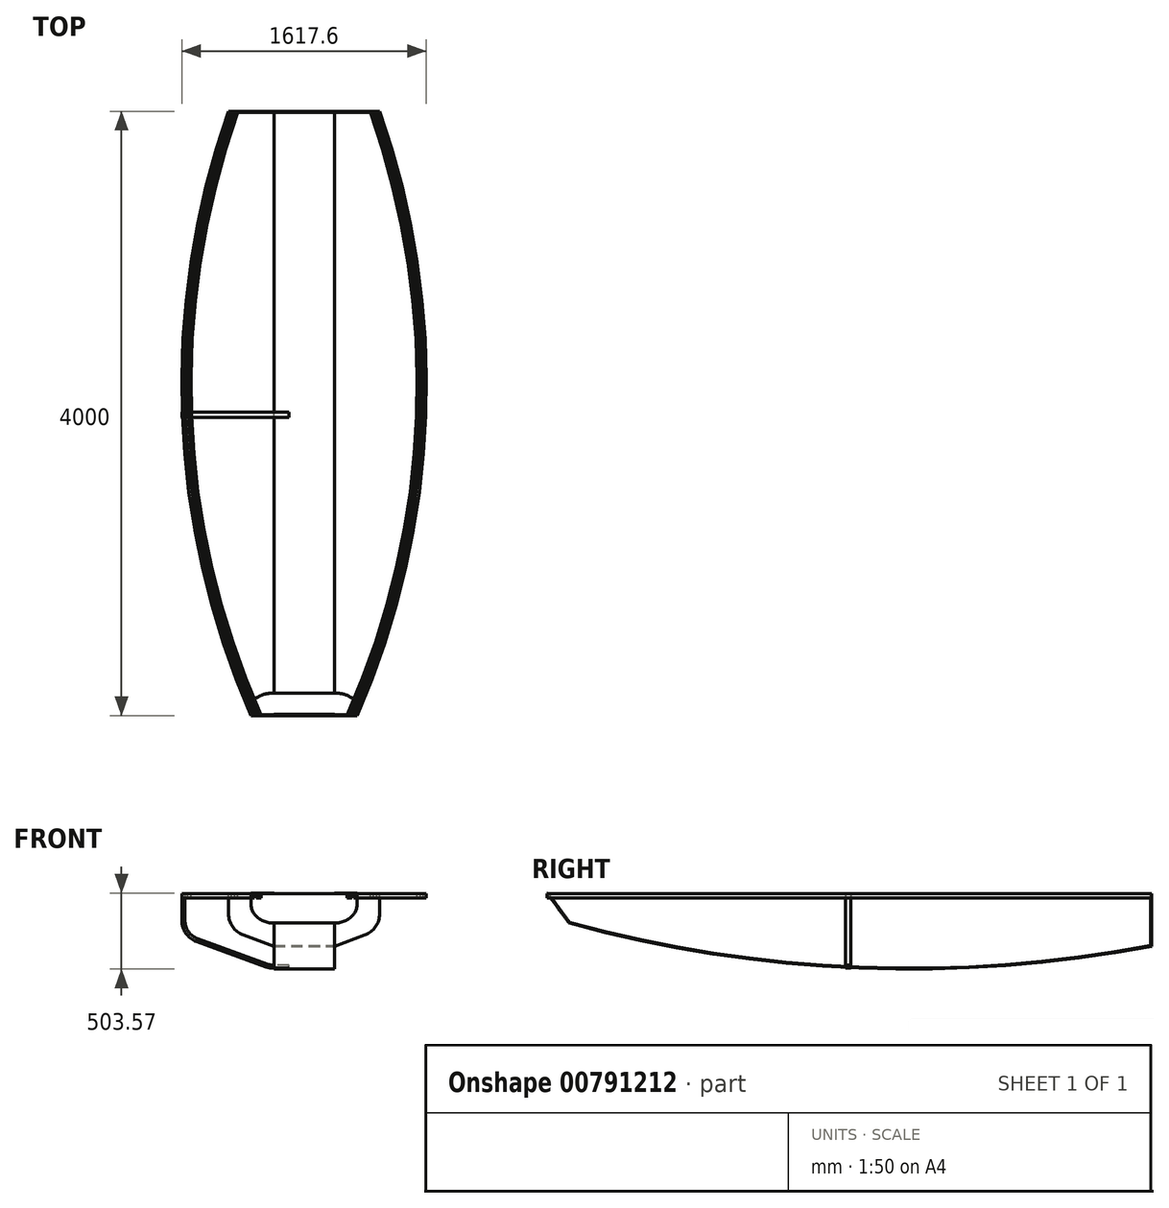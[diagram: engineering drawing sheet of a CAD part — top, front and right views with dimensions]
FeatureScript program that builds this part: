
annotation { "Feature Type Name" : "Feature", "Feature Type Description" : "" }
export const myFeature = defineFeature(function(context is Context, id is Id, definition is map)
    precondition{}
    {
        {
            var Q0;
            Q0=qCreatedBy(makeId("Right.planeOp"),FACE);
            var sketch = newSketch(context, id + "F0", { "sketchPlane" : qUnion([Q0])});
            skLineSegment(sketch, "E0.bottom", {"start": v(0, 0) * mm, "end": v(-4000, 0) * mm});
            skLineSegment(sketch, "E0.top", {"start": v(0, 500) * mm, "end": v(-4000, 500) * mm});
            skLineSegment(sketch, "E0.left", {"start": v(0, 0) * mm, "end": v(0, 500) * mm});
            skLineSegment(sketch, "E0.right", {"start": v(-4000, 0) * mm, "end": v(-4000, 500) * mm});
            skSolve(sketch);
        }
        {
            var Q0;
            Q0 = qSketchRegion(id + "F0", true);
            extrude(context, id + "F1", {"entities" : qUnion([Q0]), "depth" : 200 * mm, "offsetDistance" : 25 * mm, "hasSecondDirection" : true, "secondDirectionOppositeDirection" : true, "secondDirectionDepth" : 200 * mm});
        }
        {
            var Q0;
            Q0=makeQuery(id+"F1.opExtrude","CAP_FACE",FACE,{"disambiguationData":[OSD([sQuery(id+"F0.wireOp",EDGE,"E0.bottom"),sQuery(id+"F0.wireOp",EDGE,"E0.top"),sQuery(id+"F0.wireOp",EDGE,"E0.left"),sQuery(id+"F0.wireOp",EDGE,"E0.right")])],"isStart":false});
            var sketch = newSketch(context, id + "F2", { "sketchPlane" : qUnion([Q0])});
            skLineSegment(sketch, "E1.0", {"start": v(0, 0) * mm, "end": v(-4000, 0) * mm});
            skLineSegment(sketch, "E2.0", {"start": v(0, 0) * mm, "end": v(0, 151.95) * mm});
            skArc(sketch, "E3", {"start": v(-3855.38, 304.68) * mm, "mid": v(-1936.47, 6.66) * mm, "end": v(0, 151.95) * mm});
            skPoint(sketch, "E4.orphan", {"position": v(0, 500) * mm});
            skPoint(sketch, "E5.orphan", {"position": v(-4121.15, 382.5) * mm});
            skPoint(sketch, "E6.start.orphan", {"position": v(-4000, 500) * mm});
            skLineSegment(sketch, "E7", {"start": v(-4000, 500) * mm, "end": v(-4000, 0) * mm});
            skLineSegment(sketch, "E8", {"start": v(-3855.38, 304.68) * mm, "end": v(-4000, 500) * mm});
            skSolve(sketch);
        }
        {
            var Q0;
            Q0 = qSketchRegion(id + "F2", true);
            extrude(context, id + "F3", {"entities" : qUnion([Q0]), "operationType" : NewBodyOperationType.REMOVE, "endBound" : BoundingType.THROUGH_ALL, "oppositeDirection" : true, "depth" : 25 * mm, "offsetDistance" : 25 * mm});
        }
        {
            var Q0;
            Q0=makeQuery(id+"F1.opExtrude","CAP_FACE",FACE,{"disambiguationData":[OSD([sQuery(id+"F0.wireOp",EDGE,"E0.bottom"),sQuery(id+"F0.wireOp",EDGE,"E0.top"),sQuery(id+"F0.wireOp",EDGE,"E0.left"),sQuery(id+"F0.wireOp",EDGE,"E0.right")])],"isStart":false});
            var sketch = newSketch(context, id + "F4", { "sketchPlane" : qUnion([Q0])});
            skArc(sketch, "E9.0", {"start": v(-3851.8, 309.92) * mm, "mid": v(-1937.68, 12.71) * mm, "end": v(-6, 156.9) * mm});
            skLineSegment(sketch, "E10.0", {"start": v(-6, 156.9) * mm, "end": v(-6, 500) * mm});
            skLineSegment(sketch, "E11.0", {"start": v(-3851.8, 309.92) * mm, "end": v(-3992.53, 500) * mm});
            skLineSegment(sketch, "E12.0", {"start": v(-6, 500) * mm, "end": v(-3992.53, 500) * mm});
            skPoint(sketch, "E13.orphan", {"position": v(0, 500) * mm});
            skPoint(sketch, "E14.orphan", {"position": v(-4000, 500) * mm});
            skSolve(sketch);
        }
        {
            var Q0;
            Q0 = qSketchRegion(id + "F4", true);
            extrude(context, id + "F5", {"entities" : qUnion([Q0]), "operationType" : NewBodyOperationType.REMOVE, "endBound" : BoundingType.THROUGH_ALL, "oppositeDirection" : true, "depth" : 25 * mm, "offsetDistance" : 25 * mm});
        }
        {
            var Q0;
            Q0=qCreatedBy(makeId("Front.planeOp"),FACE);
            cPlane(context, id + "F6", {"entities" : qUnion([Q0]), "cplaneType" : CPlaneType.OFFSET, "offset" : 200 * mm, "width" : 150 * mm, "height" : 150 * mm});
        }
        {
            var Q0;
            Q0=qCreatedBy(id+"F6.planeOp",FACE);
            cPlane(context, id + "F7", {"entities" : qUnion([Q0]), "cplaneType" : CPlaneType.OFFSET, "offset" : 200 * mm, "width" : 150 * mm, "height" : 150 * mm});
        }
        {
            var Q0;
            Q0=qCreatedBy(id+"F7.planeOp",FACE);
            cPlane(context, id + "F8", {"entities" : qUnion([Q0]), "cplaneType" : CPlaneType.OFFSET, "offset" : 200 * mm, "width" : 150 * mm, "height" : 150 * mm});
        }
        {
            var Q0;
            Q0=qCreatedBy(id+"F8.planeOp",FACE);
            cPlane(context, id + "F9", {"entities" : qUnion([Q0]), "cplaneType" : CPlaneType.OFFSET, "offset" : 200 * mm, "width" : 150 * mm, "height" : 150 * mm});
        }
        {
            var Q0;
            Q0=qCreatedBy(id+"F9.planeOp",FACE);
            cPlane(context, id + "F10", {"entities" : qUnion([Q0]), "cplaneType" : CPlaneType.OFFSET, "offset" : 200 * mm, "width" : 150 * mm, "height" : 150 * mm});
        }
        {
            var Q0;
            Q0=qCreatedBy(id+"F10.planeOp",FACE);
            cPlane(context, id + "F11", {"entities" : qUnion([Q0]), "cplaneType" : CPlaneType.OFFSET, "offset" : 200 * mm, "width" : 150 * mm, "height" : 150 * mm});
        }
        {
            var Q0;
            Q0=qCreatedBy(id+"F11.planeOp",FACE);
            cPlane(context, id + "F12", {"entities" : qUnion([Q0]), "cplaneType" : CPlaneType.OFFSET, "offset" : 200 * mm, "width" : 150 * mm, "height" : 150 * mm});
        }
        {
            var Q0;
            Q0=qCreatedBy(id+"F12.planeOp",FACE);
            cPlane(context, id + "F13", {"entities" : qUnion([Q0]), "cplaneType" : CPlaneType.OFFSET, "offset" : 200 * mm, "width" : 150 * mm, "height" : 150 * mm});
        }
        {
            var Q0;
            Q0=qCreatedBy(id+"F13.planeOp",FACE);
            cPlane(context, id + "F14", {"entities" : qUnion([Q0]), "cplaneType" : CPlaneType.OFFSET, "offset" : 200 * mm, "width" : 150 * mm, "height" : 150 * mm});
        }
        {
            var Q0;
            Q0=qCreatedBy(id+"F14.planeOp",FACE);
            cPlane(context, id + "F15", {"entities" : qUnion([Q0]), "cplaneType" : CPlaneType.OFFSET, "offset" : 200 * mm, "width" : 150 * mm, "height" : 150 * mm});
        }
        {
            var Q0;
            Q0=qCreatedBy(id+"F15.planeOp",FACE);
            cPlane(context, id + "F16", {"entities" : qUnion([Q0]), "cplaneType" : CPlaneType.OFFSET, "offset" : 200 * mm, "width" : 150 * mm, "height" : 150 * mm});
        }
        {
            var Q0;
            Q0=qCreatedBy(id+"F16.planeOp",FACE);
            cPlane(context, id + "F17", {"entities" : qUnion([Q0]), "cplaneType" : CPlaneType.OFFSET, "offset" : 200 * mm, "width" : 150 * mm, "height" : 150 * mm});
        }
        {
            var Q0;
            Q0=qCreatedBy(id+"F17.planeOp",FACE);
            cPlane(context, id + "F18", {"entities" : qUnion([Q0]), "cplaneType" : CPlaneType.OFFSET, "offset" : 200 * mm, "width" : 150 * mm, "height" : 150 * mm});
        }
        {
            var Q0;
            Q0=qCreatedBy(id+"F18.planeOp",FACE);
            cPlane(context, id + "F19", {"entities" : qUnion([Q0]), "cplaneType" : CPlaneType.OFFSET, "offset" : 200 * mm, "width" : 150 * mm, "height" : 150 * mm});
        }
        {
            var Q0;
            Q0=qCreatedBy(id+"F19.planeOp",FACE);
            cPlane(context, id + "F20", {"entities" : qUnion([Q0]), "cplaneType" : CPlaneType.OFFSET, "offset" : 200 * mm, "width" : 150 * mm, "height" : 150 * mm});
        }
        {
            var Q0;
            Q0=qCreatedBy(id+"F20.planeOp",FACE);
            cPlane(context, id + "F21", {"entities" : qUnion([Q0]), "cplaneType" : CPlaneType.OFFSET, "offset" : 200 * mm, "width" : 150 * mm, "height" : 150 * mm});
        }
        {
            var Q0;
            Q0=qCreatedBy(id+"F21.planeOp",FACE);
            cPlane(context, id + "F22", {"entities" : qUnion([Q0]), "cplaneType" : CPlaneType.OFFSET, "offset" : 200 * mm, "width" : 150 * mm, "height" : 150 * mm});
        }
        {
            var Q0;
            Q0=qCreatedBy(id+"F22.planeOp",FACE);
            cPlane(context, id + "F23", {"entities" : qUnion([Q0]), "cplaneType" : CPlaneType.OFFSET, "offset" : 200 * mm, "width" : 150 * mm, "height" : 150 * mm});
        }
        {
            var Q0;
            Q0=qCreatedBy(makeId("Top.planeOp"),FACE);
            cPlane(context, id + "F24", {"entities" : qUnion([Q0]), "cplaneType" : CPlaneType.OFFSET, "offset" : 500 * mm, "width" : 150 * mm, "height" : 150 * mm});
        }
        {
            var Q0;
            Q0=makeQuery(id+"F3.boolean.opBoolean","COPY",FACE,{"derivedFrom":makeQuery(id+"F3.opExtrude","SWEPT_FACE",FACE,{"disambiguationData":[OSD([sQuery(id+"F2.wireOp",EDGE,"E8")])]})});
            var sketch = newSketch(context, id + "F25", { "sketchPlane" : qUnion([Q0])});
            skLineSegment(sketch, "E15.0.3", {"start": v(200, 2539.04) * mm, "end": v(-200, 2539.04) * mm});
            skLineSegment(sketch, "E16.0", {"start": v(-200, 2539.04) * mm, "end": v(-200, 2782.07) * mm});
            skLineSegment(sketch, "E17", {"start": v(-200, 2782.07) * mm, "end": v(-350, 2782.07) * mm});
            skPoint(sketch, "E15.0.1.end.orphan", {"position": v(200, 122.12) * mm});
            skPoint(sketch, "E15.0.1.start.orphan", {"position": v(-200, 122.12) * mm});
            skArc(sketch, "E18", {"start": v(-200, 2539.04) * mm, "mid": v(-306.07, 2582.97) * mm, "end": v(-350, 2689.04) * mm});
            skLineSegment(sketch, "E19", {"start": v(-200, 2689.04) * mm, "end": v(-440.1, 2689.04) * mm, "construction": true});
            skLineSegment(sketch, "E20", {"start": v(-350, 2689.04) * mm, "end": v(-350, 2782.07) * mm});
            skSolve(sketch);
        }
        {
            var Q0;
            Q0 = qSketchRegion(id + "F25", true);
            extrude(context, id + "F26", {"entities" : qUnion([Q0]), "oppositeDirection" : true, "depth" : 6 * mm, "offsetDistance" : 25 * mm});
        }
        {
            var Q0;
            Q0=makeQuery(id+"F26.opExtrude","SWEPT_BODY",BODY,{"disambiguationData":[OSD([sQuery(id+"F25.wireOp",EDGE,"E16.0"),sQuery(id+"F25.wireOp",EDGE,"E17"),sQuery(id+"F25.wireOp",EDGE,"E18"),sQuery(id+"F25.wireOp",EDGE,"E20")])]});
            var Q1;
            Q1=qCreatedBy(makeId("Right.planeOp"),FACE);
            mirror(context, id + "F27", {"operationType" : NewBodyOperationType.ADD, "entities" : qUnion([Q0]), "mirrorPlane" : qUnion([Q1])});
        }
        {
            var Q0;
            Q0=qCreatedBy(id+"F24.planeOp",FACE);
            var sketch = newSketch(context, id + "F28", { "sketchPlane" : qUnion([Q0])});
            skLineSegment(sketch, "E21", {"start": v(-436.36, 0) * mm, "end": v(-457.58, 0) * mm});
            skLineSegment(sketch, "E22", {"start": v(0, 0) * mm, "end": v(0, -4123.04) * mm, "construction": true});
            skLineSegment(sketch, "E23.0", {"start": v(-200, -4000) * mm, "end": v(-326.44, -4000) * mm, "construction": true});
            skLineSegment(sketch, "E24", {"start": v(0, -1500) * mm, "end": v(-800, -1500) * mm, "construction": true});
            skArc(sketch, "E25", {"start": v(-500, 0) * mm, "mid": v(-804.96, -2014.25) * mm, "end": v(-350, -4000) * mm});
            skArc(sketch, "E26.0", {"start": v(-478.8, 0) * mm, "mid": v(-682.4, -739.35) * mm, "end": v(-779.97, -1500) * mm});
            skArc(sketch, "E27.0", {"start": v(-457.58, 0) * mm, "mid": v(-764.93, -2014.48) * mm, "end": v(-306.3, -4000) * mm});
            skArc(sketch, "E28.0", {"start": v(-436.36, 0) * mm, "mid": v(-744.9, -2014.6) * mm, "end": v(-284.42, -4000) * mm});
            skLineSegment(sketch, "E29", {"start": v(-284.42, -4000) * mm, "end": v(-306.3, -4000) * mm});
            skLineSegment(sketch, "E30.trimOffspring", {"start": v(-478.8, 0) * mm, "end": v(-500, 0) * mm});
            skLineSegment(sketch, "E31", {"start": v(-350, -4000) * mm, "end": v(-326.44, -4000) * mm});
            skArc(sketch, "E32.0", {"start": v(-779.97, -1500) * mm, "mid": v(-702.12, -2776.76) * mm, "end": v(-328.16, -4000) * mm});
            skLineSegment(sketch, "E33.trimOffspring", {"start": v(-328.16, -4000) * mm, "end": v(-350, -4000) * mm, "construction": true});
            skSolve(sketch);
        }
        {
            var Q0;
            Q0 = qSketchRegion(id + "F28", true);
            extrude(context, id + "F29", {"entities" : qUnion([Q0]), "oppositeDirection" : true, "depth" : 30 * mm, "offsetDistance" : 25 * mm});
        }
        {
            var Q0;
            Q0=makeQuery(id+"F29.opExtrude","SWEPT_BODY",BODY,{"disambiguationData":[OSD([sQuery(id+"F28.wireOp",EDGE,"E25"),sQuery(id+"F28.wireOp",EDGE,"E26.0"),sQuery(id+"F28.wireOp",EDGE,"JQv3v1hN-lLp6-lVGY-2l0k-aHUHcDUw9ejT"),sQuery(id+"F28.wireOp",EDGE,"E30.trimOffspring")])]});
            var Q1;
            Q1=makeQuery(id+"F29.opExtrude","SWEPT_BODY",BODY,{"disambiguationData":[OSD([sQuery(id+"F28.wireOp",EDGE,"E21"),sQuery(id+"F28.wireOp",EDGE,"E27.0"),sQuery(id+"F28.wireOp",EDGE,"E28.0"),sQuery(id+"F28.wireOp",EDGE,"E29")])]});
            var Q2;
            Q2=qCreatedBy(makeId("Right.planeOp"),FACE);
            mirror(context, id + "F30", {"operationType" : NewBodyOperationType.ADD, "entities" : qUnion([Q0, Q1]), "mirrorPlane" : qUnion([Q2])});
        }
        {
            var Q0;
            Q0=qCreatedBy(makeId("Front.planeOp"),FACE);
            var sketch = newSketch(context, id + "F31", { "sketchPlane" : qUnion([Q0])});
            skLineSegment(sketch, "E34.0", {"start": v(200, 151.95) * mm, "end": v(200, 500) * mm});
            skLineSegment(sketch, "E35.0", {"start": v(-200, 151.95) * mm, "end": v(200, 151.95) * mm, "construction": true});
            skLineSegment(sketch, "E36.0", {"start": v(500, 470) * mm, "end": v(500, 500) * mm});
            skLineSegment(sketch, "E37", {"start": v(500, 470) * mm, "end": v(500, 366.17) * mm});
            skLineSegment(sketch, "E38", {"start": v(500, 366.17) * mm, "end": v(350, 366.17) * mm, "construction": true});
            skArc(sketch, "E39", {"start": v(401.3, 225.21) * mm, "mid": v(472.87, 280.13) * mm, "end": v(500, 366.17) * mm});
            skLineSegment(sketch, "E40", {"start": v(200, 151.95) * mm, "end": v(401.3, 225.21) * mm});
            skLineSegment(sketch, "E41", {"start": v(500, 500) * mm, "end": v(200, 500) * mm});
            skSolve(sketch);
        }
        {
            var Q0;
            Q0 = qSketchRegion(id + "F31", true);
            extrude(context, id + "F32", {"entities" : qUnion([Q0]), "depth" : 6 * mm, "offsetDistance" : 25 * mm});
        }
        {
            var Q0;
            Q0=makeQuery(id+"F32.opExtrude","SWEPT_BODY",BODY,{"disambiguationData":[OSD([sQuery(id+"F31.wireOp",EDGE,"E34.0"),sQuery(id+"F31.wireOp",EDGE,"E36.0"),sQuery(id+"F31.wireOp",EDGE,"E37"),sQuery(id+"F31.wireOp",EDGE,"E39"),sQuery(id+"F31.wireOp",EDGE,"E40"),sQuery(id+"F31.wireOp",EDGE,"E41")])]});
            var Q1;
            Q1=qCreatedBy(makeId("Right.planeOp"),FACE);
            mirror(context, id + "F33", {"operationType" : NewBodyOperationType.ADD, "entities" : qUnion([Q0]), "mirrorPlane" : qUnion([Q1])});
        }
        {
            var Q0;
            Q0=qCreatedBy(id+"F15.planeOp",FACE);
            var sketch = newSketch(context, id + "F34", { "sketchPlane" : qUnion([Q0])});
            skLineSegment(sketch, "E42", {"start": v(-100, 6) * mm, "end": v(-200, 6) * mm});
            skLineSegment(sketch, "E43", {"start": v(-100, 6) * mm, "end": v(-100, 26) * mm});
            skLineSegment(sketch, "E44.0", {"start": v(-100, 26) * mm, "end": v(-200, 26) * mm});
            skLineSegment(sketch, "E45", {"start": v(-200, 6) * mm, "end": v(-200, 156) * mm, "construction": true});
            skLineSegment(sketch, "E46", {"start": v(-200, 156) * mm, "end": v(-282.27, -70.04) * mm, "construction": true});
            skArc(sketch, "E47", {"start": v(-251.3, 15.05) * mm, "mid": v(-226.05, 8.28) * mm, "end": v(-200, 6) * mm});
            skArc(sketch, "E48.0", {"start": v(-244.46, 33.84) * mm, "mid": v(-222.57, 27.97) * mm, "end": v(-200, 26) * mm});
            skLineSegment(sketch, "E49", {"start": v(-808.8, 470) * mm, "end": v(-808.8, 500) * mm});
            skLineSegment(sketch, "E50", {"start": v(-808.8, 470) * mm, "end": v(-808.8, 322.99) * mm});
            skLineSegment(sketch, "E51.0", {"start": v(-788.8, 500) * mm, "end": v(-788.8, 297.72) * mm});
            skLineSegment(sketch, "E52", {"start": v(-808.8, 500) * mm, "end": v(-788.8, 500) * mm});
            skLineSegment(sketch, "E53", {"start": v(-808.8, 322.99) * mm, "end": v(-658.8, 322.99) * mm, "construction": true});
            skArc(sketch, "E54", {"start": v(-808.8, 322.99) * mm, "mid": v(-781.67, 236.95) * mm, "end": v(-710.1, 182.03) * mm});
            skLineSegment(sketch, "E55", {"start": v(-251.3, 15.05) * mm, "end": v(-710.1, 182.03) * mm});
            skArc(sketch, "E56.0", {"start": v(-788.8, 322.99) * mm, "mid": v(-765.29, 248.42) * mm, "end": v(-703.26, 200.83) * mm});
            skLineSegment(sketch, "E57.0", {"start": v(-244.46, 33.84) * mm, "end": v(-703.26, 200.83) * mm});
            skSolve(sketch);
        }
        {
            var Q0;
            Q0 = qSketchRegion(id + "F34", true);
            extrude(context, id + "F35", {"entities" : qUnion([Q0]), "depth" : 25 * mm, "offsetDistance" : 25 * mm, "hasSecondDirection" : true, "secondDirectionOppositeDirection" : true, "secondDirectionDepth" : 10 * mm});
        }
    });
